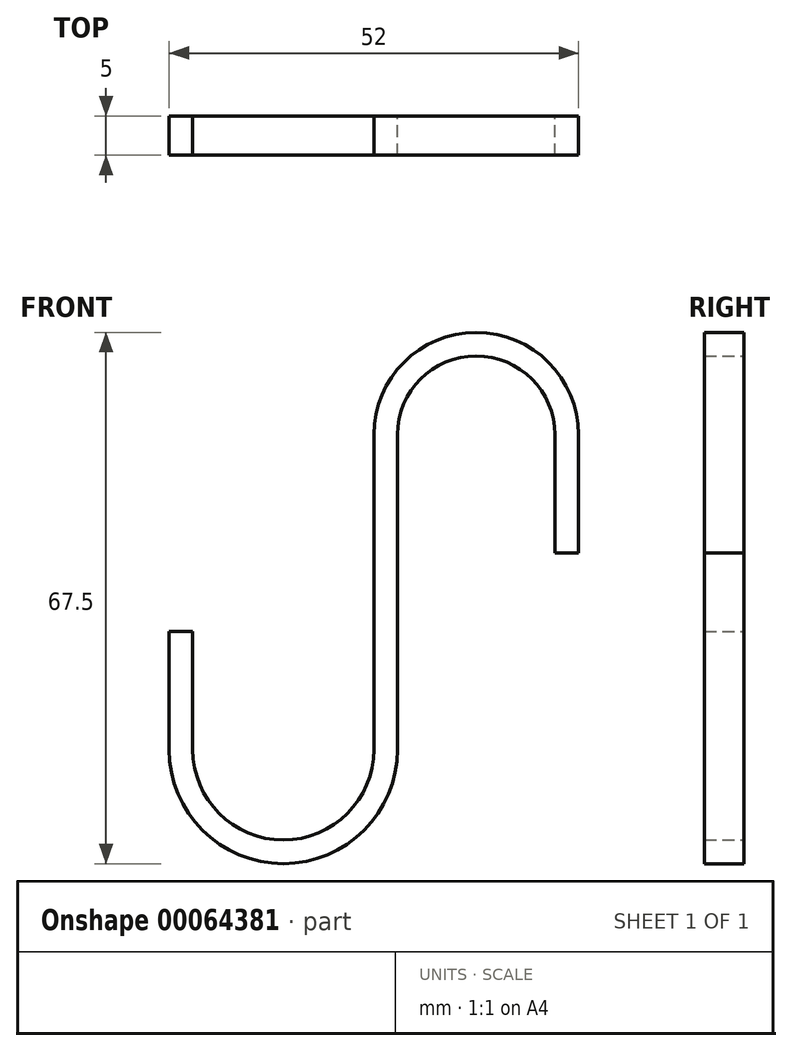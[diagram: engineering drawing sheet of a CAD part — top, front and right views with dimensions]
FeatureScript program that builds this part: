
annotation { "Feature Type Name" : "Feature", "Feature Type Description" : "" }
export const myFeature = defineFeature(function(context is Context, id is Id, definition is map)
    precondition{}
    {
        {
            var Q0;
            Q0=qCreatedBy(makeId("Front.planeOp"),FACE);
            var sketch = newSketch(context, id + "F0", { "sketchPlane" : qUnion([Q0])});
            skLineSegment(sketch, "E0", {"start": v(23, 5) * mm, "end": v(23, 20) * mm});
            skLineSegment(sketch, "E1", {"start": v(3, 0) * mm, "end": v(3, 20) * mm});
            skArc(sketch, "E2", {"start": v(3, 20) * mm, "mid": v(13, 30) * mm, "end": v(23, 20) * mm});
            skLineSegment(sketch, "E3.0", {"start": v(0, 0) * mm, "end": v(0, 20) * mm});
            skArc(sketch, "E3.1", {"start": v(0, 20) * mm, "mid": v(13, 33) * mm, "end": v(26, 20) * mm});
            skLineSegment(sketch, "E3.2", {"start": v(26, 5) * mm, "end": v(26, 20) * mm});
            skLineSegment(sketch, "E4", {"start": v(26, 5) * mm, "end": v(23, 5) * mm});
            skLineSegment(sketch, "E5", {"start": v(3, 0) * mm, "end": v(0, 0) * mm});
            skLineSegment(sketch, "E6", {"start": v(0, 0) * mm, "end": v(0, -20) * mm});
            skLineSegment(sketch, "E7", {"start": v(-23, -5) * mm, "end": v(-23, -20) * mm});
            skArc(sketch, "E8", {"start": v(0, -20) * mm, "mid": v(-11.5, -31.5) * mm, "end": v(-23, -20) * mm});
            skLineSegment(sketch, "E9.0", {"start": v(3, 0) * mm, "end": v(3, -20) * mm});
            skArc(sketch, "E9.1", {"start": v(3, -20) * mm, "mid": v(-11.5, -34.5) * mm, "end": v(-26, -20) * mm});
            skLineSegment(sketch, "E9.2", {"start": v(-26, -5) * mm, "end": v(-26, -20) * mm});
            skLineSegment(sketch, "E10", {"start": v(-23, -5) * mm, "end": v(-26, -5) * mm});
            skSolve(sketch);
        }
        {
            assignVariable(context, id + "F1", {"name" : "width", "anyValue" : 5});
        }
        {
            var Q0;
            Q0=makeQuery(id+"F0.imprint","IMPRINT",FACE,{"disambiguationData":[TD([[makeQuery(id+"F0.imprint","IMPRINT",EDGE,{"derivedFrom":sQuery(id+"F0.wireOp",EDGE,"E0")}),-1.0]])]});
            var Q1;
            Q1=makeQuery(id+"F0.imprint","IMPRINT",FACE,{"disambiguationData":[TD([[makeQuery(id+"F0.imprint","IMPRINT",EDGE,{"derivedFrom":sQuery(id+"F0.wireOp",EDGE,"E5")}),1.0]])]});
            extrude(context, id + "F2", {"entities" : qUnion([Q0, Q1]), "depth" : (getVariable(context, 'width')) * mm});
        }
    });
